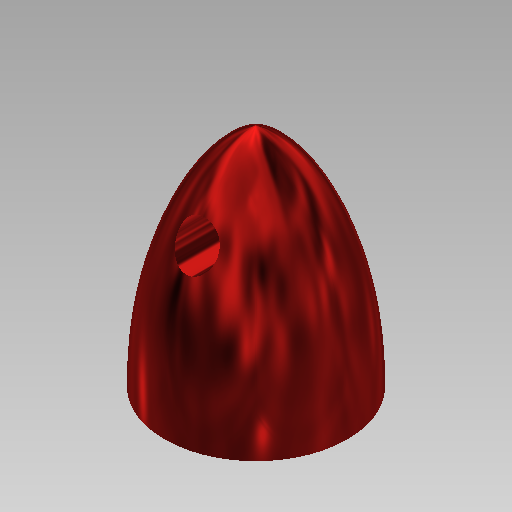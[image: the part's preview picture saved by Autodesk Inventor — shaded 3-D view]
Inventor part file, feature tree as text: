
AUTODESK INVENTOR PART (.ipt)
format: ipt  version: 2018.1 (Build 221171000, 171)  size: 233,984 bytes
history: native  units: in
note: dims shown in document units (in); Inventor stores cm internally (conversion verified against a paired STEP export)
features: sketch x3, extrude x2, revolve x1, chamfer x1, thread x1
ambient origin geometry x8: Origin, YZ Plane, XZ Plane, XY Plane, X Axis, Y Axis, Z Axis, Center Point
bodies: Solid1 (feature_tree)
feature tree (8):
  revolve  "Revolution1"  [1 undecoded]
  extrude  "Extrusion1"  Depth=0.5118in TaperAngle=0.0deg
  extrude  "Extrusion3"  Depth=0.3937in TaperAngle=0.0deg
  chamfer  "Chamfer1"  [1 undecoded]
  thread  "Thread6"  [1 undecoded]
  sketch  "Sketch1"  dims[d3=90.0deg d6=0.5906in d7=0.0in]
  sketch  "Sketch2"  dims[d8=0.1969in d28=0.5118in d29=0.0in]
  sketch  "Sketch3"  dims[d30=0.0197in d31=0.0787in d32=45.0deg d33=0.3937in d34=0.0in]
note: 3 required parameter values undecoded (feature->parameter linkage not recoverable at this tier; creation-order binding heuristic only, values carry confidence <= 0.55)